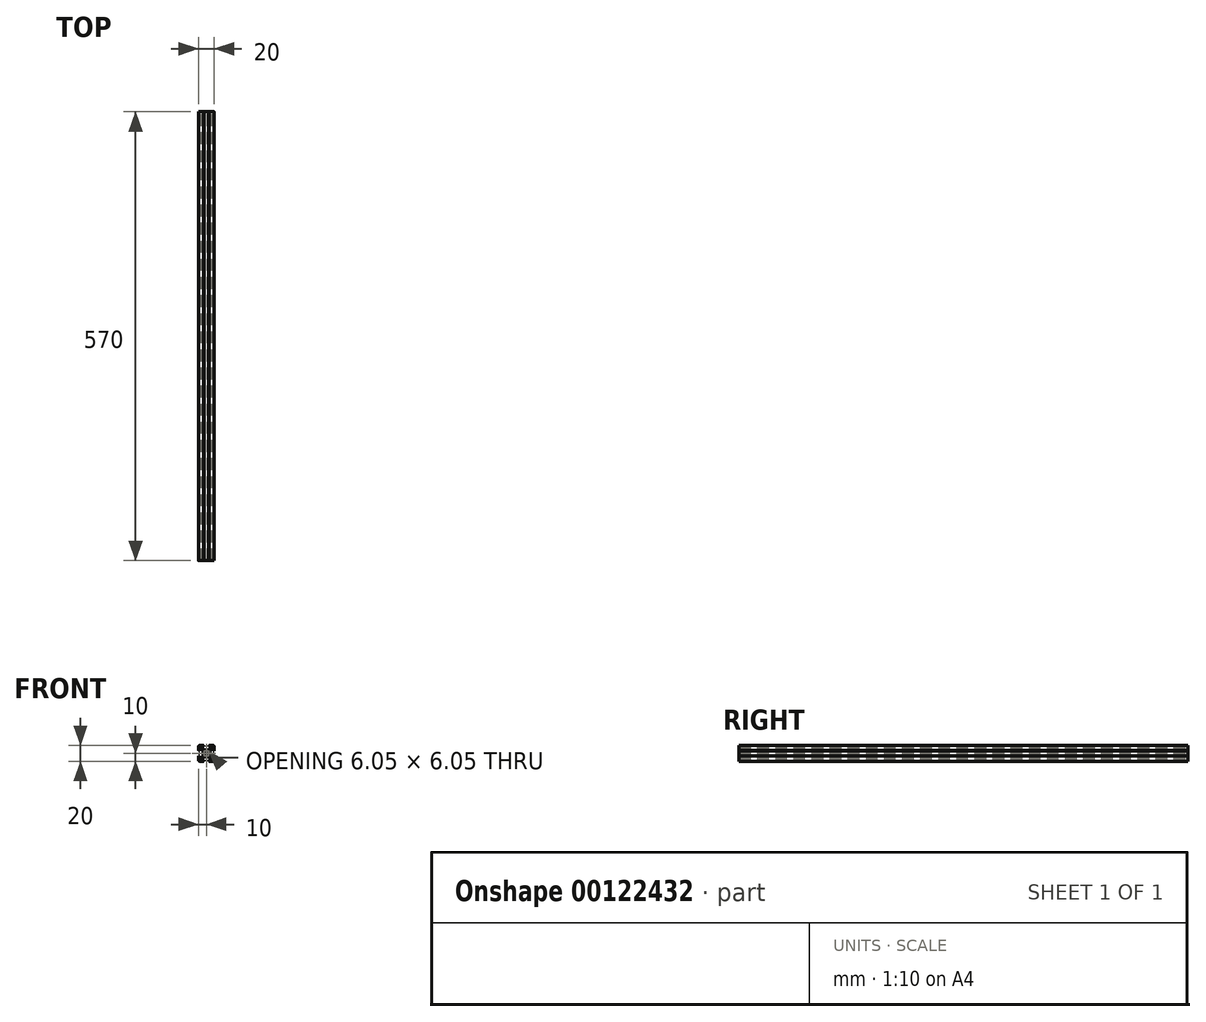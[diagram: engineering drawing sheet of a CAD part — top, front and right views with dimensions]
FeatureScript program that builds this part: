
annotation { "Feature Type Name" : "Feature", "Feature Type Description" : "" }
export const myFeature = defineFeature(function(context is Context, id is Id, definition is map)
    precondition{}
    {
        {
            var Q0;
            Q0=qCreatedBy(makeId("Front.planeOp"),FACE);
            var sketch = newSketch(context, id + "F0", { "sketchPlane" : qUnion([Q0])});
            skLineSegment(sketch, "E0", {"start": v(0, 4.5) * mm, "end": v(3.44, 4.5) * mm});
            skLineSegment(sketch, "E1", {"start": v(3.44, 4.5) * mm, "end": v(6, 7.06) * mm});
            skLineSegment(sketch, "E2", {"start": v(6, 7.06) * mm, "end": v(6, 8.5) * mm});
            skLineSegment(sketch, "E3", {"start": v(6, 8.5) * mm, "end": v(3, 8.5) * mm});
            skLineSegment(sketch, "E4", {"start": v(3, 8.5) * mm, "end": v(3, 9.5) * mm});
            skLineSegment(sketch, "E5", {"start": v(3, 9.5) * mm, "end": v(3.5, 9.5) * mm});
            skLineSegment(sketch, "E6", {"start": v(3.5, 9.5) * mm, "end": v(3.5, 10) * mm});
            skLineSegment(sketch, "E7", {"start": v(3.5, 10) * mm, "end": v(8.5, 10) * mm});
            skLineSegment(sketch, "E8", {"start": v(0, 0) * mm, "end": v(11.95, 11.95) * mm, "construction": true});
            skLineSegment(sketch, "E9.MirrorCS", {"start": v(9.5, 3) * mm, "end": v(9.5, 3.5) * mm});
            skLineSegment(sketch, "E10.MirrorCS", {"start": v(9.5, 3.5) * mm, "end": v(10, 3.5) * mm});
            skLineSegment(sketch, "E11.MirrorCS", {"start": v(4.5, 3.44) * mm, "end": v(7.06, 6) * mm});
            skLineSegment(sketch, "E12.MirrorCS", {"start": v(7.06, 6) * mm, "end": v(8.5, 6) * mm});
            skLineSegment(sketch, "E13.MirrorCS", {"start": v(8.5, 6) * mm, "end": v(8.5, 3) * mm});
            skLineSegment(sketch, "E14.MirrorCS", {"start": v(8.5, 3) * mm, "end": v(9.5, 3) * mm});
            skLineSegment(sketch, "E15.MirrorCS", {"start": v(10, 3.5) * mm, "end": v(10, 8.5) * mm});
            skLineSegment(sketch, "E16.MirrorCS", {"start": v(4.5, 0) * mm, "end": v(4.5, 3.44) * mm});
            skPoint(sketch, "E17.visualSharp", {"position": v(10, 10) * mm});
            skArc(sketch, "E17.filletArc", {"start": v(10, 8.5) * mm, "mid": v(9.56, 9.56) * mm, "end": v(8.5, 10) * mm});
            skArc(sketch, "E18", {"start": v(0, 2.75) * mm, "mid": v(0.7, 2.66) * mm, "end": v(1.34, 2.4) * mm});
            skLineSegment(sketch, "E19", {"start": v(1.34, 2.4) * mm, "end": v(1.96, 3.02) * mm});
            skLineSegment(sketch, "E20", {"start": v(1.96, 3.02) * mm, "end": v(3.02, 1.96) * mm});
            skLineSegment(sketch, "E21", {"start": v(3.02, 1.96) * mm, "end": v(2.4, 1.34) * mm});
            skArc(sketch, "E22.trimOffspring", {"start": v(2.4, 1.34) * mm, "mid": v(2.66, 0.7) * mm, "end": v(2.75, 0) * mm});
            skLineSegment(sketch, "E23.MirrorCS", {"start": v(1.96, 3.02) * mm, "end": v(1.34, 2.4) * mm});
            skLineSegment(sketch, "E24.MirrorCS", {"start": v(2.4, 1.34) * mm, "end": v(3.02, 1.96) * mm});
            skArc(sketch, "E25.MirrorCS", {"start": v(8.5, 10) * mm, "mid": v(9.56, 9.56) * mm, "end": v(10, 8.5) * mm});
            skArc(sketch, "E26.MirrorCS", {"start": v(2.75, 0) * mm, "mid": v(2.66, 0.7) * mm, "end": v(2.4, 1.34) * mm});
            skArc(sketch, "E27.MirrorCS", {"start": v(1.34, 2.4) * mm, "mid": v(0.7, 2.66) * mm, "end": v(0, 2.75) * mm});
            skLineSegment(sketch, "E28.MirrorCS", {"start": v(3.02, 1.96) * mm, "end": v(1.96, 3.02) * mm});
            skLineSegment(sketch, "E29.MirrorCS", {"start": v(3, -9.5) * mm, "end": v(3.5, -9.5) * mm});
            skLineSegment(sketch, "E30.MirrorCS", {"start": v(9.5, -3) * mm, "end": v(9.5, -3.5) * mm});
            skLineSegment(sketch, "E31.MirrorCS", {"start": v(9.5, -3.5) * mm, "end": v(10, -3.5) * mm});
            skLineSegment(sketch, "E32.MirrorCS", {"start": v(3.5, -9.5) * mm, "end": v(3.5, -10) * mm});
            skLineSegment(sketch, "E33.MirrorCS", {"start": v(6, -7.06) * mm, "end": v(6, -8.5) * mm});
            skArc(sketch, "E34.MirrorCS", {"start": v(8.5, -10) * mm, "mid": v(9.56, -9.56) * mm, "end": v(10, -8.5) * mm});
            skLineSegment(sketch, "E35.MirrorCS", {"start": v(3.5, -10) * mm, "end": v(8.5, -10) * mm});
            skLineSegment(sketch, "E36.MirrorCS", {"start": v(0, -4.5) * mm, "end": v(3.44, -4.5) * mm});
            skLineSegment(sketch, "E37.MirrorCS", {"start": v(3.02, -1.96) * mm, "end": v(1.96, -3.02) * mm});
            skLineSegment(sketch, "E38.MirrorCS", {"start": v(1.34, -2.4) * mm, "end": v(1.96, -3.02) * mm});
            skLineSegment(sketch, "E39.MirrorCS", {"start": v(4.5, -3.44) * mm, "end": v(7.06, -6) * mm});
            skLineSegment(sketch, "E40.MirrorCS", {"start": v(7.06, -6) * mm, "end": v(8.5, -6) * mm});
            skLineSegment(sketch, "E41.MirrorCS", {"start": v(3.44, -4.5) * mm, "end": v(6, -7.06) * mm});
            skLineSegment(sketch, "E42.MirrorCS", {"start": v(6, -8.5) * mm, "end": v(3, -8.5) * mm});
            skLineSegment(sketch, "E43.MirrorCS", {"start": v(8.5, -6) * mm, "end": v(8.5, -3) * mm});
            skLineSegment(sketch, "E44.MirrorCS", {"start": v(10, -3.5) * mm, "end": v(10, -8.5) * mm});
            skLineSegment(sketch, "E45.MirrorCS", {"start": v(8.5, -3) * mm, "end": v(9.5, -3) * mm});
            skLineSegment(sketch, "E46.MirrorCS", {"start": v(3.02, -1.96) * mm, "end": v(2.4, -1.34) * mm});
            skLineSegment(sketch, "E47.MirrorCS", {"start": v(4.5, 0) * mm, "end": v(4.5, -3.44) * mm});
            skLineSegment(sketch, "E48.MirrorCS", {"start": v(3, -8.5) * mm, "end": v(3, -9.5) * mm});
            skPoint(sketch, "E49.MirrorP", {"position": v(10, -10) * mm});
            skLineSegment(sketch, "E50.MirrorCS", {"start": v(1.96, -3.02) * mm, "end": v(3.02, -1.96) * mm});
            skLineSegment(sketch, "E51.MirrorCS", {"start": v(1.96, -3.02) * mm, "end": v(1.34, -2.4) * mm});
            skArc(sketch, "E52.MirrorCS", {"start": v(10, -8.5) * mm, "mid": v(9.56, -9.56) * mm, "end": v(8.5, -10) * mm});
            skArc(sketch, "E53.MirrorCS", {"start": v(0, -2.75) * mm, "mid": v(0.7, -2.66) * mm, "end": v(1.34, -2.4) * mm});
            skArc(sketch, "E54.MirrorCS", {"start": v(2.75, 0) * mm, "mid": v(2.66, -0.7) * mm, "end": v(2.4, -1.34) * mm});
            skArc(sketch, "E55.MirrorCS", {"start": v(2.4, -1.34) * mm, "mid": v(2.66, -0.7) * mm, "end": v(2.75, 0) * mm});
            skLineSegment(sketch, "E56.MirrorCS", {"start": v(2.4, -1.34) * mm, "end": v(3.02, -1.96) * mm});
            skArc(sketch, "E57.MirrorCS", {"start": v(1.34, -2.4) * mm, "mid": v(0.7, -2.66) * mm, "end": v(0, -2.75) * mm});
            skLineSegment(sketch, "E58.MirrorCS", {"start": v(-1.34, 2.4) * mm, "end": v(-1.96, 3.02) * mm});
            skLineSegment(sketch, "E59.MirrorCS", {"start": v(-9.5, 3) * mm, "end": v(-9.5, 3.5) * mm});
            skLineSegment(sketch, "E60.MirrorCS", {"start": v(-9.5, -3) * mm, "end": v(-9.5, -3.5) * mm});
            skLineSegment(sketch, "E61.MirrorCS", {"start": v(-3.02, 1.96) * mm, "end": v(-2.4, 1.34) * mm});
            skLineSegment(sketch, "E62.MirrorCS", {"start": v(-3.5, 9.5) * mm, "end": v(-3.5, 10) * mm});
            skLineSegment(sketch, "E63.MirrorCS", {"start": v(-3, -9.5) * mm, "end": v(-3.5, -9.5) * mm});
            skLineSegment(sketch, "E64.MirrorCS", {"start": v(-1.34, -2.4) * mm, "end": v(-1.96, -3.02) * mm});
            skLineSegment(sketch, "E65.MirrorCS", {"start": v(-3, 9.5) * mm, "end": v(-3.5, 9.5) * mm});
            skLineSegment(sketch, "E66.MirrorCS", {"start": v(-9.5, -3.5) * mm, "end": v(-10, -3.5) * mm});
            skLineSegment(sketch, "E67.MirrorCS", {"start": v(-9.5, 3.5) * mm, "end": v(-10, 3.5) * mm});
            skLineSegment(sketch, "E68.MirrorCS", {"start": v(-3.02, -1.96) * mm, "end": v(-2.4, -1.34) * mm});
            skLineSegment(sketch, "E69.MirrorCS", {"start": v(-3.5, -9.5) * mm, "end": v(-3.5, -10) * mm});
            skLineSegment(sketch, "E70.MirrorCS", {"start": v(-1.96, -3.02) * mm, "end": v(-1.34, -2.4) * mm});
            skLineSegment(sketch, "E71.MirrorCS", {"start": v(-2.4, -1.34) * mm, "end": v(-3.02, -1.96) * mm});
            skLineSegment(sketch, "E72.MirrorCS", {"start": v(-1.96, 3.02) * mm, "end": v(-1.34, 2.4) * mm});
            skLineSegment(sketch, "E73.MirrorCS", {"start": v(-2.4, 1.34) * mm, "end": v(-3.02, 1.96) * mm});
            skLineSegment(sketch, "E74.MirrorCS", {"start": v(-3.5, 10) * mm, "end": v(-8.5, 10) * mm});
            skLineSegment(sketch, "E75.MirrorCS", {"start": v(-8.5, 6) * mm, "end": v(-8.5, 3) * mm});
            skLineSegment(sketch, "E76.MirrorCS", {"start": v(-6, 8.5) * mm, "end": v(-3, 8.5) * mm});
            skLineSegment(sketch, "E77.MirrorCS", {"start": v(-3, 8.5) * mm, "end": v(-3, 9.5) * mm});
            skLineSegment(sketch, "E78.MirrorCS", {"start": v(-3.5, -10) * mm, "end": v(-8.5, -10) * mm});
            skLineSegment(sketch, "E79.MirrorCS", {"start": v(-6, 7.06) * mm, "end": v(-6, 8.5) * mm});
            skLineSegment(sketch, "E80.MirrorCS", {"start": v(-3, -8.5) * mm, "end": v(-3, -9.5) * mm});
            skPoint(sketch, "E81.MirrorP", {"position": v(-10, -10) * mm});
            skLineSegment(sketch, "E82.MirrorCS", {"start": v(-4.5, 3.44) * mm, "end": v(-7.06, 6) * mm});
            skLineSegment(sketch, "E83.MirrorCS", {"start": v(-7.06, 6) * mm, "end": v(-8.5, 6) * mm});
            skLineSegment(sketch, "E84.MirrorCS", {"start": v(-3.44, 4.5) * mm, "end": v(-6, 7.06) * mm});
            skLineSegment(sketch, "E85.MirrorCS", {"start": v(-10, -3.5) * mm, "end": v(-10, -8.5) * mm});
            skLineSegment(sketch, "E86.MirrorCS", {"start": v(-7.06, -6) * mm, "end": v(-8.5, -6) * mm});
            skLineSegment(sketch, "E87.MirrorCS", {"start": v(-8.5, -6) * mm, "end": v(-8.5, -3) * mm});
            skLineSegment(sketch, "E88.MirrorCS", {"start": v(-4.5, 0) * mm, "end": v(-4.5, -3.44) * mm});
            skLineSegment(sketch, "E89.MirrorCS", {"start": v(-4.5, -3.44) * mm, "end": v(-7.06, -6) * mm});
            skLineSegment(sketch, "E90.MirrorCS", {"start": v(-1.96, 3.02) * mm, "end": v(-3.02, 1.96) * mm});
            skLineSegment(sketch, "E91.MirrorCS", {"start": v(-4.5, 0) * mm, "end": v(-4.5, 3.44) * mm});
            skLineSegment(sketch, "E92.MirrorCS", {"start": v(0, -4.5) * mm, "end": v(-3.44, -4.5) * mm});
            skLineSegment(sketch, "E93.MirrorCS", {"start": v(-6, -7.06) * mm, "end": v(-6, -8.5) * mm});
            skArc(sketch, "E94.MirrorCS", {"start": v(-8.5, 10) * mm, "mid": v(-9.56, 9.56) * mm, "end": v(-10, 8.5) * mm});
            skLineSegment(sketch, "E95.MirrorCS", {"start": v(-10, 3.5) * mm, "end": v(-10, 8.5) * mm});
            skPoint(sketch, "E96.MirrorP", {"position": v(-10, 10) * mm});
            skLineSegment(sketch, "E97.MirrorCS", {"start": v(-6, -8.5) * mm, "end": v(-3, -8.5) * mm});
            skArc(sketch, "E98.MirrorCS", {"start": v(-8.5, -10) * mm, "mid": v(-9.56, -9.56) * mm, "end": v(-10, -8.5) * mm});
            skLineSegment(sketch, "E99.MirrorCS", {"start": v(0, 4.5) * mm, "end": v(-3.44, 4.5) * mm});
            skLineSegment(sketch, "E100.MirrorCS", {"start": v(-8.5, 3) * mm, "end": v(-9.5, 3) * mm});
            skLineSegment(sketch, "E101.MirrorCS", {"start": v(-1.96, -3.02) * mm, "end": v(-3.02, -1.96) * mm});
            skLineSegment(sketch, "E102.MirrorCS", {"start": v(-8.5, -3) * mm, "end": v(-9.5, -3) * mm});
            skLineSegment(sketch, "E103.MirrorCS", {"start": v(-3.44, -4.5) * mm, "end": v(-6, -7.06) * mm});
            skLineSegment(sketch, "E104.MirrorCS", {"start": v(-3.02, -1.96) * mm, "end": v(-1.96, -3.02) * mm});
            skArc(sketch, "E105.MirrorCS", {"start": v(-10, 8.5) * mm, "mid": v(-9.56, 9.56) * mm, "end": v(-8.5, 10) * mm});
            skArc(sketch, "E106.MirrorCS", {"start": v(-10, -8.5) * mm, "mid": v(-9.56, -9.56) * mm, "end": v(-8.5, -10) * mm});
            skLineSegment(sketch, "E107.MirrorCS", {"start": v(-3.02, 1.96) * mm, "end": v(-1.96, 3.02) * mm});
            skArc(sketch, "E108.MirrorCS", {"start": v(0, -2.75) * mm, "mid": v(-0.7, -2.66) * mm, "end": v(-1.34, -2.4) * mm});
            skArc(sketch, "E109.MirrorCS", {"start": v(-1.34, -2.4) * mm, "mid": v(-0.7, -2.66) * mm, "end": v(0, -2.75) * mm});
            skArc(sketch, "E110.MirrorCS", {"start": v(0, 2.75) * mm, "mid": v(-0.7, 2.66) * mm, "end": v(-1.34, 2.4) * mm});
            skArc(sketch, "E111.MirrorCS", {"start": v(-2.75, 0) * mm, "mid": v(-2.66, -0.7) * mm, "end": v(-2.4, -1.34) * mm});
            skArc(sketch, "E112.MirrorCS", {"start": v(-2.75, 0) * mm, "mid": v(-2.66, 0.7) * mm, "end": v(-2.4, 1.34) * mm});
            skArc(sketch, "E113.MirrorCS", {"start": v(-2.4, 1.34) * mm, "mid": v(-2.66, 0.7) * mm, "end": v(-2.75, 0) * mm});
            skArc(sketch, "E114.MirrorCS", {"start": v(-1.34, 2.4) * mm, "mid": v(-0.7, 2.66) * mm, "end": v(0, 2.75) * mm});
            skArc(sketch, "E115.MirrorCS", {"start": v(-2.4, -1.34) * mm, "mid": v(-2.66, -0.7) * mm, "end": v(-2.75, 0) * mm});
            skSolve(sketch);
        }
        {
            var Q0;
            Q0 = qSketchRegion(id + "F0", true);
            extrude(context, id + "F1", {"entities" : qUnion([Q0]), "depth" : 570 * mm});
        }
    });
